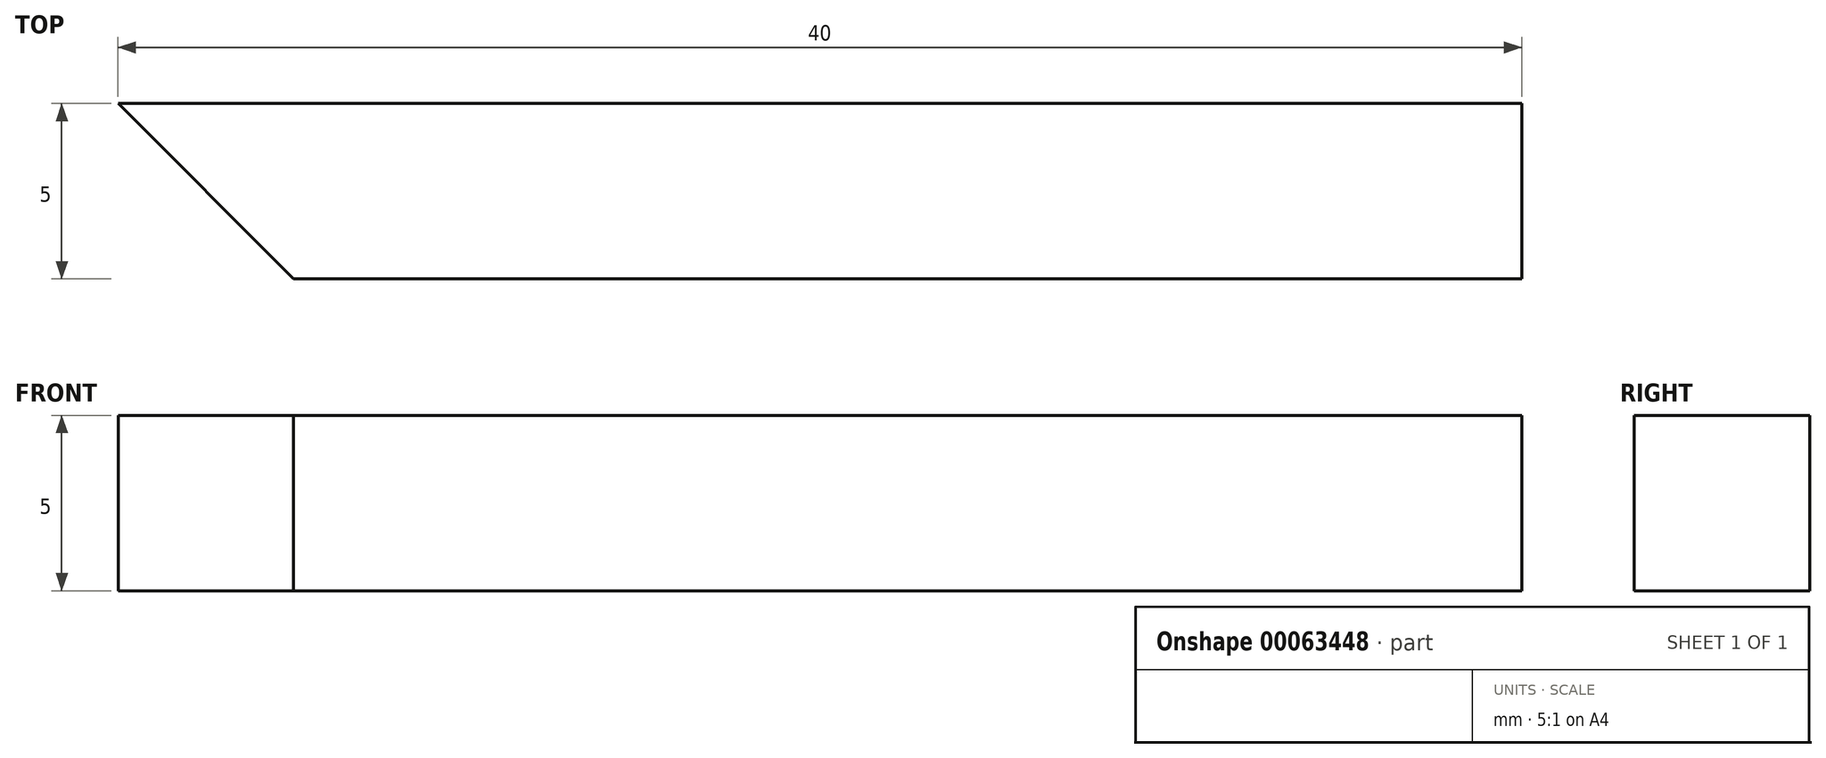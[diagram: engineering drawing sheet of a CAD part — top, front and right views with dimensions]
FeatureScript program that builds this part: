
annotation { "Feature Type Name" : "Feature", "Feature Type Description" : "" }
export const myFeature = defineFeature(function(context is Context, id is Id, definition is map)
    precondition{}
    {
        {
            var Q0;
            Q0=qCreatedBy(makeId("Top.planeOp"),FACE);
            var sketch = newSketch(context, id + "F0", { "sketchPlane" : qUnion([Q0])});
            skLineSegment(sketch, "E0", {"start": v(-9.26, 5) * mm, "end": v(30.74, 5) * mm});
            skLineSegment(sketch, "E1", {"start": v(30.74, 5) * mm, "end": v(30.74, 0) * mm});
            skLineSegment(sketch, "E2", {"start": v(30.74, 0) * mm, "end": v(-4.26, 0) * mm});
            skLineSegment(sketch, "E3", {"start": v(-4.26, 0) * mm, "end": v(-9.26, 5) * mm});
            skSolve(sketch);
        }
        {
            var Q0;
            Q0 = qSketchRegion(id + "F0", true);
            extrude(context, id + "F1", {"entities" : qUnion([Q0]), "depth" : 5 * mm});
        }
    });
